# Revit family: S90-SPOT BL 2000 DALI 930 15°_Unhosted
name_source: partatom
category: Lighting Fixtures
revit_build: Autodesk Revit 2016 (Build: 20161004_0715(x64)
units: mm (PartAtom-declared; Revit-internal decimal feet)

## family parameters
Always vertical = Yes
Cut with Voids When Loaded = No
Light Source = Yes
OmniClass Number = 23.80.70.00
OmniClass Title = Lighting
Part Type = Normal
Room Calculation Point = No
Round Connector Dimension = Use Diameter
Shared = No
Work Plane-Based = Yes

## types (1)
- S90-SPOT BL 2000 DALI 930 15°_Unhosted
    # ballast on a MCB16 type B fuse = 60
    #Ballast = 1
    #Tubes = 1
    Apparent Load = 17 VA
    ArticleNumber = S90225514
    Body Material and Colour = Default
    Color Filter = 16777215
    Default Elevation = 1800 mm  [stored 5.90551 ft]
    Description = S90-SPOT BL 2000 DALI 930 15°
    Dimming Lamp Color Temperature Shift = <None>
    EANNo = 7020940420921
    Emit Shape Visible in Rendering = No
    Emit from Circle Diameter = 80 mm  [stored 0.262467 ft]
    Expired = 0
    Frequency = 50 Hz
    FrequencyMax = 60 Hz
    Glamox Category = Spotlights
    Glamox Family = S90-SPOT
    Glamox Mounting = Surface
    GlobalTradeItemNumber = 7020940420921
    Height = 157 mm  [stored 0.515092 ft]
    IFC Classification = Light Fixture
    IPClass = 20
    IP_Code = 20
    Lamp = LED
    LightFixtureMountingType = TRACKMOUNTED
    LightFixturePlacingType = CEILING
    LumLenght = 80 mm  [stored 0.262467 ft]
    MFArtNo = S90225514
    MaintenanceFactor = 0
    Manufacturer = Glamox
    ModelLabel = S90-SPOT BL 2000 DALI 930 15°
    ModelReference = S90-SPOT
    NominalFrequencyRange = 50 Hz
    Number of Poles = 1
    NumberOfSources = 1
    Photometric Web File = S90-SPOT-2000-DALI-930-15.ies
    Power Factor = 0.98
    Power factor = 0.98
    PowerFactor = 98.00%
    RatedVoltage = 220 V
    Specification = Spotlight luminaries, in Aluminium, for Surface/Track mounting, IP20, light source LED, lumen out 2310lm, ballast type DALI.
    Tilt Angle = 90.00°
    Total Load = 19 W
    TotalWattage = 19 W
    TypeOfBallast = DALI
    URL Denmark = http://glamox.com
    URL Estonia = http://glamox.com
    URL Finland = http://glamox.com
    URL Germany = http://glamox.com
    URL Ireland = http://glamox.com
    URL Norway = http://glamox.com
    URL Other = http://glamox.com
    URL Russia = http://glamox.com
    URL Sweden = http://glamox.com
    URL UK = http://glamox.com
    UpdateDate = 16.10.2020 07:42:45
    Voltage = 220 V
    VoltageMax = 240 V
    Width = 100 mm  [stored 0.328084 ft]

note: [stored X ft] marks values corroborated as IEEE doubles in the binary element streams (Revit-internal decimal feet)

## geometry (parser evidence)
native form markers: Blend x4, Sweep x1
no freeform markers — native parametric forms only
